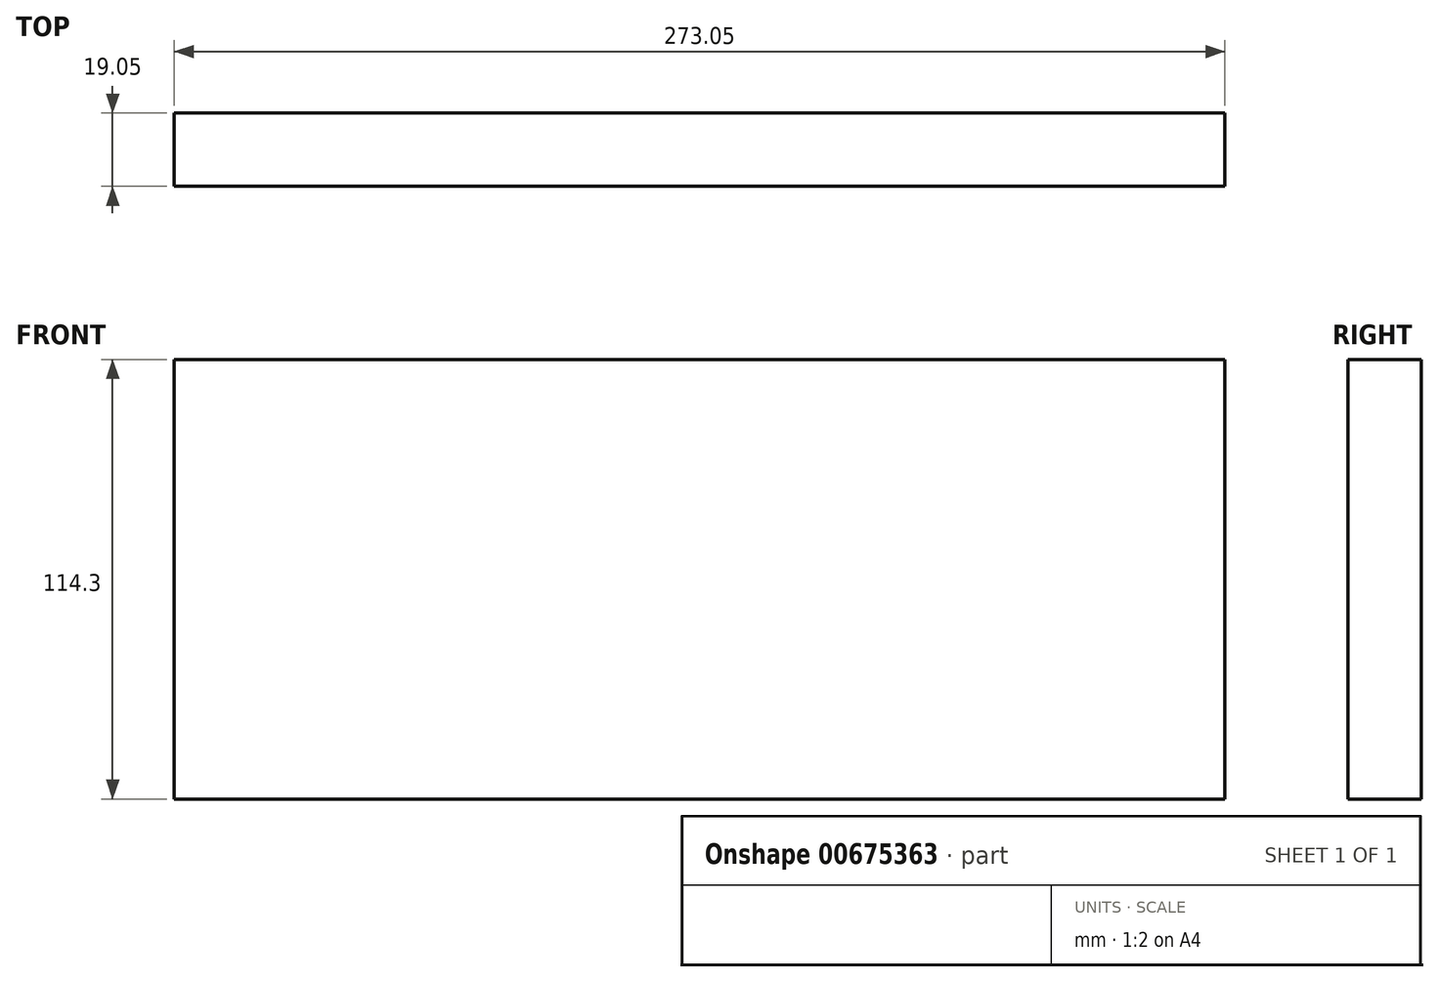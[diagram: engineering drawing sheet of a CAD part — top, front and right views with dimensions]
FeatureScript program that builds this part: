
annotation { "Feature Type Name" : "Feature", "Feature Type Description" : "" }
export const myFeature = defineFeature(function(context is Context, id is Id, definition is map)
    precondition{}
    {
        {
            var Q0;
            Q0=qCreatedBy(makeId("Front.planeOp"),FACE);
            var sketch = newSketch(context, id + "F0", { "sketchPlane" : qUnion([Q0])});
            skLineSegment(sketch, "E0.bottom", {"start": v(0, 16.18) * mm, "end": v(273.05, 16.18) * mm});
            skLineSegment(sketch, "E0.top", {"start": v(0, 130.48) * mm, "end": v(273.05, 130.48) * mm});
            skLineSegment(sketch, "E0.left", {"start": v(0, 16.18) * mm, "end": v(0, 130.48) * mm});
            skLineSegment(sketch, "E0.right", {"start": v(273.05, 16.18) * mm, "end": v(273.05, 130.48) * mm});
            skSolve(sketch);
        }
        {
            var Q0;
            Q0 = qSketchRegion(id + "F0", true);
            extrude(context, id + "F1", {"entities" : qUnion([Q0]), "depth" : 19.05 * mm, "offsetDistance" : 25.4 * mm});
        }
    });
